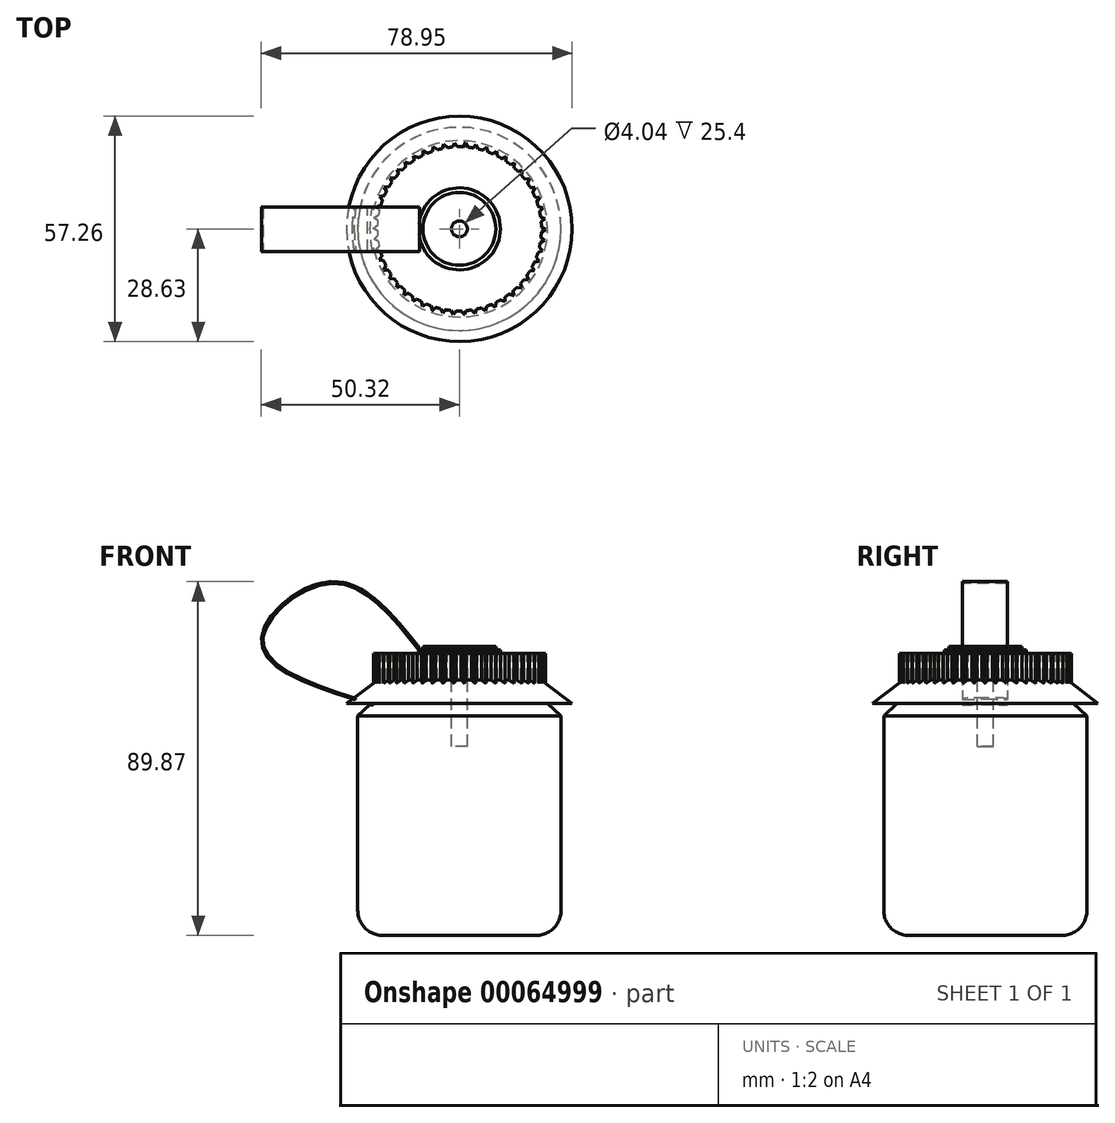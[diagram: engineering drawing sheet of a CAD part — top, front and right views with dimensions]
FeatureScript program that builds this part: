
annotation { "Feature Type Name" : "Feature", "Feature Type Description" : "" }
export const myFeature = defineFeature(function(context is Context, id is Id, definition is map)
    precondition{}
    {
        {
            var Q0;
            Q0=qCreatedBy(makeId("Front.planeOp"),FACE);
            var sketch = newSketch(context, id + "F0", { "sketchPlane" : qUnion([Q0])});
            skLineSegment(sketch, "E0", {"start": v(0, 0) * mm, "end": v(0, -55.76) * mm});
            skLineSegment(sketch, "E1", {"start": v(0, -55.76) * mm, "end": v(-19.47, -55.76) * mm});
            skLineSegment(sketch, "E2", {"start": v(-25.82, -49.41) * mm, "end": v(-25.82, 0) * mm});
            skLineSegment(sketch, "E3", {"start": v(0, 15.82) * mm, "end": v(0, 0) * mm});
            skPoint(sketch, "E4.visualSharp", {"position": v(-25.82, -55.76) * mm});
            skArc(sketch, "E4.filletArc", {"start": v(-25.82, -49.41) * mm, "mid": v(-23.96, -53.9) * mm, "end": v(-19.47, -55.76) * mm});
            skLineSegment(sketch, "E5", {"start": v(-25.82, 0) * mm, "end": v(-22.4, 3.12) * mm});
            skLineSegment(sketch, "E6", {"start": v(-22.4, 3.12) * mm, "end": v(-28.63, 3.12) * mm});
            skLineSegment(sketch, "E7", {"start": v(-28.63, 3.12) * mm, "end": v(-20.78, 9.12) * mm});
            skLineSegment(sketch, "E8", {"start": v(-20.78, 9.12) * mm, "end": v(-20.78, 15.82) * mm});
            skLineSegment(sketch, "E9", {"start": v(-20.78, 15.82) * mm, "end": v(0, 15.82) * mm});
            skSolve(sketch);
        }
        {
            var Q0;
            Q0 = qSketchRegion(id + "F0", true);
            var Q1;
            Q1=sQuery(id+"F0.wireOp",EDGE,"E0");
            revolve(context, id + "F1", {"entities" : qUnion([Q0]), "axis" : qUnion([Q1]), "revolveType" : RevolveType.FULL});
        }
        {
            var Q0;
            Q0=makeQuery(id+"F1.opRevolve","SWEPT_FACE",FACE,{"disambiguationData":[OSD([sQuery(id+"F0.wireOp",EDGE,"E9")])]});
            var sketch = newSketch(context, id + "F2", { "sketchPlane" : qUnion([Q0])});
            skCircle(sketch, "E10", {"center": v(0, 0) * mm, "radius": 20.84 * mm});
            skLineSegment(sketch, "E11", {"start": v(18.63, 9.2) * mm, "end": v(19.22, 10.42) * mm});
            skLineSegment(sketch, "E12", {"start": v(19.22, 10.42) * mm, "end": v(17.98, 10.42) * mm});
            skLineSegment(sketch, "E13.1.0", {"start": v(17.33, 11.47) * mm, "end": v(17.76, 12.75) * mm});
            skLineSegment(sketch, "E13.1.1", {"start": v(17.76, 12.75) * mm, "end": v(16.53, 12.6) * mm});
            skLineSegment(sketch, "E13.2.0", {"start": v(15.76, 13.55) * mm, "end": v(16.03, 14.88) * mm});
            skLineSegment(sketch, "E13.2.1", {"start": v(16.03, 14.88) * mm, "end": v(14.82, 14.57) * mm});
            skLineSegment(sketch, "E13.3.0", {"start": v(13.93, 15.42) * mm, "end": v(14.04, 16.77) * mm});
            skLineSegment(sketch, "E13.3.1", {"start": v(14.04, 16.77) * mm, "end": v(12.88, 16.31) * mm});
            skLineSegment(sketch, "E13.4.0", {"start": v(11.9, 17.04) * mm, "end": v(11.82, 18.4) * mm});
            skLineSegment(sketch, "E13.4.1", {"start": v(11.82, 18.4) * mm, "end": v(10.73, 17.8) * mm});
            skLineSegment(sketch, "E13.5.0", {"start": v(9.66, 18.4) * mm, "end": v(9.42, 19.73) * mm});
            skLineSegment(sketch, "E13.5.1", {"start": v(9.42, 19.73) * mm, "end": v(8.42, 19) * mm});
            skLineSegment(sketch, "E13.6.0", {"start": v(7.28, 19.47) * mm, "end": v(6.88, 20.76) * mm});
            skLineSegment(sketch, "E13.6.1", {"start": v(6.88, 20.76) * mm, "end": v(5.97, 19.9) * mm});
            skLineSegment(sketch, "E13.7.0", {"start": v(4.78, 20.22) * mm, "end": v(4.22, 21.46) * mm});
            skLineSegment(sketch, "E13.7.1", {"start": v(4.22, 21.46) * mm, "end": v(3.43, 20.5) * mm});
            skLineSegment(sketch, "E13.8.0", {"start": v(2.2, 20.66) * mm, "end": v(1.5, 21.82) * mm});
            skLineSegment(sketch, "E13.8.1", {"start": v(1.5, 21.82) * mm, "end": v(0.83, 20.77) * mm});
            skLineSegment(sketch, "E13.9.0", {"start": v(-0.4, 20.78) * mm, "end": v(-1.25, 21.83) * mm});
            skLineSegment(sketch, "E13.9.1", {"start": v(-1.25, 21.83) * mm, "end": v(-1.78, 20.7) * mm});
            skLineSegment(sketch, "E13.10.0", {"start": v(-3, 20.56) * mm, "end": v(-3.97, 21.5) * mm});
            skLineSegment(sketch, "E13.10.1", {"start": v(-3.97, 21.5) * mm, "end": v(-4.36, 20.32) * mm});
            skLineSegment(sketch, "E13.11.0", {"start": v(-5.55, 20.03) * mm, "end": v(-6.64, 20.84) * mm});
            skLineSegment(sketch, "E13.11.1", {"start": v(-6.64, 20.84) * mm, "end": v(-6.87, 19.61) * mm});
            skLineSegment(sketch, "E13.12.0", {"start": v(-8.02, 19.17) * mm, "end": v(-9.2, 19.84) * mm});
            skLineSegment(sketch, "E13.12.1", {"start": v(-9.2, 19.84) * mm, "end": v(-9.27, 18.6) * mm});
            skLineSegment(sketch, "E13.13.0", {"start": v(-10.36, 18.02) * mm, "end": v(-11.61, 18.53) * mm});
            skLineSegment(sketch, "E13.13.1", {"start": v(-11.61, 18.53) * mm, "end": v(-11.53, 17.29) * mm});
            skLineSegment(sketch, "E13.14.0", {"start": v(-12.54, 16.58) * mm, "end": v(-13.84, 16.93) * mm});
            skLineSegment(sketch, "E13.14.1", {"start": v(-13.84, 16.93) * mm, "end": v(-13.6, 15.7) * mm});
            skLineSegment(sketch, "E13.15.0", {"start": v(-14.51, 14.87) * mm, "end": v(-15.85, 15.06) * mm});
            skLineSegment(sketch, "E13.15.1", {"start": v(-15.85, 15.06) * mm, "end": v(-15.47, 13.88) * mm});
            skLineSegment(sketch, "E13.16.0", {"start": v(-16.26, 12.94) * mm, "end": v(-17.62, 12.95) * mm});
            skLineSegment(sketch, "E13.16.1", {"start": v(-17.62, 12.95) * mm, "end": v(-17.09, 11.83) * mm});
            skLineSegment(sketch, "E13.17.0", {"start": v(-17.76, 10.8) * mm, "end": v(-19.1, 10.64) * mm});
            skLineSegment(sketch, "E13.17.1", {"start": v(-19.1, 10.64) * mm, "end": v(-18.43, 9.6) * mm});
            skLineSegment(sketch, "E13.18.0", {"start": v(-18.97, 8.49) * mm, "end": v(-20.29, 8.17) * mm});
            skLineSegment(sketch, "E13.18.1", {"start": v(-20.29, 8.17) * mm, "end": v(-19.5, 7.2) * mm});
            skLineSegment(sketch, "E13.19.0", {"start": v(-19.88, 6.04) * mm, "end": v(-21.15, 5.56) * mm});
            skLineSegment(sketch, "E13.19.1", {"start": v(-21.15, 5.56) * mm, "end": v(-20.24, 4.7) * mm});
            skLineSegment(sketch, "E13.20.0", {"start": v(-20.48, 3.5) * mm, "end": v(-21.68, 2.87) * mm});
            skLineSegment(sketch, "E13.20.1", {"start": v(-21.68, 2.87) * mm, "end": v(-20.67, 2.13) * mm});
            skLineSegment(sketch, "E13.21.0", {"start": v(-20.76, 0.9) * mm, "end": v(-21.87, 0.13) * mm});
            skLineSegment(sketch, "E13.21.1", {"start": v(-21.87, 0.13) * mm, "end": v(-20.78, -0.47) * mm});
            skLineSegment(sketch, "E13.22.0", {"start": v(-20.71, -1.7) * mm, "end": v(-21.71, -2.62) * mm});
            skLineSegment(sketch, "E13.22.1", {"start": v(-21.71, -2.62) * mm, "end": v(-20.55, -3.07) * mm});
            skLineSegment(sketch, "E13.23.0", {"start": v(-20.34, -4.29) * mm, "end": v(-21.21, -5.32) * mm});
            skLineSegment(sketch, "E13.23.1", {"start": v(-21.21, -5.32) * mm, "end": v(-20, -5.63) * mm});
            skLineSegment(sketch, "E13.24.0", {"start": v(-19.64, -6.8) * mm, "end": v(-20.38, -7.93) * mm});
            skLineSegment(sketch, "E13.24.1", {"start": v(-20.38, -7.93) * mm, "end": v(-19.14, -8.09) * mm});
            skLineSegment(sketch, "E13.25.0", {"start": v(-18.63, -9.2) * mm, "end": v(-19.22, -10.42) * mm});
            skLineSegment(sketch, "E13.25.1", {"start": v(-19.22, -10.42) * mm, "end": v(-17.98, -10.42) * mm});
            skLineSegment(sketch, "E13.26.0", {"start": v(-17.33, -11.47) * mm, "end": v(-17.76, -12.75) * mm});
            skLineSegment(sketch, "E13.26.1", {"start": v(-17.76, -12.75) * mm, "end": v(-16.53, -12.6) * mm});
            skLineSegment(sketch, "E13.27.0", {"start": v(-15.76, -13.55) * mm, "end": v(-16.03, -14.88) * mm});
            skLineSegment(sketch, "E13.27.1", {"start": v(-16.03, -14.88) * mm, "end": v(-14.82, -14.57) * mm});
            skLineSegment(sketch, "E13.28.0", {"start": v(-13.93, -15.42) * mm, "end": v(-14.04, -16.77) * mm});
            skLineSegment(sketch, "E13.28.1", {"start": v(-14.04, -16.77) * mm, "end": v(-12.88, -16.31) * mm});
            skLineSegment(sketch, "E13.29.0", {"start": v(-11.9, -17.04) * mm, "end": v(-11.82, -18.4) * mm});
            skLineSegment(sketch, "E13.29.1", {"start": v(-11.82, -18.4) * mm, "end": v(-10.73, -17.8) * mm});
            skLineSegment(sketch, "E13.30.0", {"start": v(-9.66, -18.4) * mm, "end": v(-9.42, -19.73) * mm});
            skLineSegment(sketch, "E13.30.1", {"start": v(-9.42, -19.73) * mm, "end": v(-8.42, -19) * mm});
            skLineSegment(sketch, "E13.31.0", {"start": v(-7.28, -19.47) * mm, "end": v(-6.88, -20.76) * mm});
            skLineSegment(sketch, "E13.31.1", {"start": v(-6.88, -20.76) * mm, "end": v(-5.97, -19.9) * mm});
            skLineSegment(sketch, "E13.32.0", {"start": v(-4.78, -20.22) * mm, "end": v(-4.22, -21.46) * mm});
            skLineSegment(sketch, "E13.32.1", {"start": v(-4.22, -21.46) * mm, "end": v(-3.43, -20.5) * mm});
            skLineSegment(sketch, "E13.33.0", {"start": v(-2.2, -20.66) * mm, "end": v(-1.5, -21.82) * mm});
            skLineSegment(sketch, "E13.33.1", {"start": v(-1.5, -21.82) * mm, "end": v(-0.83, -20.77) * mm});
            skLineSegment(sketch, "E13.34.0", {"start": v(0.4, -20.78) * mm, "end": v(1.25, -21.83) * mm});
            skLineSegment(sketch, "E13.34.1", {"start": v(1.25, -21.83) * mm, "end": v(1.78, -20.7) * mm});
            skLineSegment(sketch, "E13.35.0", {"start": v(3, -20.56) * mm, "end": v(3.97, -21.5) * mm});
            skLineSegment(sketch, "E13.35.1", {"start": v(3.97, -21.5) * mm, "end": v(4.36, -20.32) * mm});
            skLineSegment(sketch, "E13.36.0", {"start": v(5.55, -20.03) * mm, "end": v(6.64, -20.84) * mm});
            skLineSegment(sketch, "E13.36.1", {"start": v(6.64, -20.84) * mm, "end": v(6.87, -19.61) * mm});
            skLineSegment(sketch, "E13.37.0", {"start": v(8.02, -19.17) * mm, "end": v(9.2, -19.84) * mm});
            skLineSegment(sketch, "E13.37.1", {"start": v(9.2, -19.84) * mm, "end": v(9.27, -18.6) * mm});
            skLineSegment(sketch, "E13.38.0", {"start": v(10.36, -18.02) * mm, "end": v(11.61, -18.53) * mm});
            skLineSegment(sketch, "E13.38.1", {"start": v(11.61, -18.53) * mm, "end": v(11.53, -17.29) * mm});
            skLineSegment(sketch, "E13.39.0", {"start": v(12.54, -16.58) * mm, "end": v(13.84, -16.93) * mm});
            skLineSegment(sketch, "E13.39.1", {"start": v(13.84, -16.93) * mm, "end": v(13.6, -15.7) * mm});
            skLineSegment(sketch, "E13.40.0", {"start": v(14.51, -14.87) * mm, "end": v(15.85, -15.06) * mm});
            skLineSegment(sketch, "E13.40.1", {"start": v(15.85, -15.06) * mm, "end": v(15.47, -13.88) * mm});
            skLineSegment(sketch, "E13.41.0", {"start": v(16.26, -12.94) * mm, "end": v(17.62, -12.95) * mm});
            skLineSegment(sketch, "E13.41.1", {"start": v(17.62, -12.95) * mm, "end": v(17.09, -11.83) * mm});
            skLineSegment(sketch, "E13.42.0", {"start": v(17.76, -10.8) * mm, "end": v(19.1, -10.64) * mm});
            skLineSegment(sketch, "E13.42.1", {"start": v(19.1, -10.64) * mm, "end": v(18.43, -9.6) * mm});
            skLineSegment(sketch, "E13.43.0", {"start": v(18.97, -8.49) * mm, "end": v(20.29, -8.17) * mm});
            skLineSegment(sketch, "E13.43.1", {"start": v(20.29, -8.17) * mm, "end": v(19.5, -7.2) * mm});
            skLineSegment(sketch, "E13.44.0", {"start": v(19.88, -6.04) * mm, "end": v(21.15, -5.56) * mm});
            skLineSegment(sketch, "E13.44.1", {"start": v(21.15, -5.56) * mm, "end": v(20.24, -4.7) * mm});
            skLineSegment(sketch, "E14.1.45.0", {"start": v(20.48, -3.5) * mm, "end": v(21.68, -2.87) * mm});
            skLineSegment(sketch, "E14.3.45.0", {"start": v(21.68, -2.87) * mm, "end": v(20.67, -2.13) * mm});
            skLineSegment(sketch, "E14.1.46.0", {"start": v(20.76, -0.9) * mm, "end": v(21.87, -0.13) * mm});
            skLineSegment(sketch, "E14.3.46.0", {"start": v(21.87, -0.13) * mm, "end": v(20.78, 0.47) * mm});
            skLineSegment(sketch, "E14.1.47.0", {"start": v(20.71, 1.7) * mm, "end": v(21.71, 2.62) * mm});
            skLineSegment(sketch, "E14.3.47.0", {"start": v(21.71, 2.62) * mm, "end": v(20.55, 3.07) * mm});
            skLineSegment(sketch, "E15.1.48.0", {"start": v(20.34, 4.29) * mm, "end": v(21.21, 5.32) * mm});
            skLineSegment(sketch, "E15.3.48.0", {"start": v(21.21, 5.32) * mm, "end": v(20, 5.63) * mm});
            skLineSegment(sketch, "E15.1.49.0", {"start": v(19.64, 6.8) * mm, "end": v(20.38, 7.93) * mm});
            skLineSegment(sketch, "E15.3.49.0", {"start": v(20.38, 7.93) * mm, "end": v(19.14, 8.09) * mm});
            skSolve(sketch);
        }
        {
            var Q0;
            Q0 = qSketchRegion(id + "F2", true);
            extrude(context, id + "F3", {"entities" : qUnion([Q0]), "operationType" : NewBodyOperationType.ADD, "oppositeDirection" : true, "depth" : 25.4 * mm});
        }
        {
            var Q0;
            Q0=makeQuery(id+"F3.boolean.opBoolean","MERGE",FACE,{"derivedFrom":[makeQuery(id+"F1.opRevolve","SWEPT_FACE",FACE,{"disambiguationData":[OSD([sQuery(id+"F0.wireOp",EDGE,"E9")])]}),makeQuery(id+"F3.opExtrude","CAP_FACE",FACE,{"disambiguationData":[OSD([sQuery(id+"F2.wireOp",EDGE,"E10"),sQuery(id+"F2.wireOp",EDGE,"E11"),sQuery(id+"F2.wireOp",EDGE,"E12"),sQuery(id+"F2.wireOp",EDGE,"E13.1.0"),sQuery(id+"F2.wireOp",EDGE,"E13.1.1"),sQuery(id+"F2.wireOp",EDGE,"E13.2.0"),sQuery(id+"F2.wireOp",EDGE,"E13.2.1"),sQuery(id+"F2.wireOp",EDGE,"E13.3.0"),sQuery(id+"F2.wireOp",EDGE,"E13.3.1"),sQuery(id+"F2.wireOp",EDGE,"E13.4.0"),sQuery(id+"F2.wireOp",EDGE,"E13.4.1"),sQuery(id+"F2.wireOp",EDGE,"E13.5.0"),sQuery(id+"F2.wireOp",EDGE,"E13.5.1"),sQuery(id+"F2.wireOp",EDGE,"E13.6.0"),sQuery(id+"F2.wireOp",EDGE,"E13.6.1"),sQuery(id+"F2.wireOp",EDGE,"E13.7.0"),sQuery(id+"F2.wireOp",EDGE,"E13.7.1"),sQuery(id+"F2.wireOp",EDGE,"E13.8.0"),sQuery(id+"F2.wireOp",EDGE,"E13.8.1"),sQuery(id+"F2.wireOp",EDGE,"E13.9.0"),sQuery(id+"F2.wireOp",EDGE,"E13.9.1"),sQuery(id+"F2.wireOp",EDGE,"E13.10.0"),sQuery(id+"F2.wireOp",EDGE,"E13.10.1"),sQuery(id+"F2.wireOp",EDGE,"E13.11.0"),sQuery(id+"F2.wireOp",EDGE,"E13.11.1"),sQuery(id+"F2.wireOp",EDGE,"E13.12.0"),sQuery(id+"F2.wireOp",EDGE,"E13.12.1"),sQuery(id+"F2.wireOp",EDGE,"E13.13.0"),sQuery(id+"F2.wireOp",EDGE,"E13.13.1"),sQuery(id+"F2.wireOp",EDGE,"E13.14.0"),sQuery(id+"F2.wireOp",EDGE,"E13.14.1"),sQuery(id+"F2.wireOp",EDGE,"E13.15.0"),sQuery(id+"F2.wireOp",EDGE,"E13.15.1"),sQuery(id+"F2.wireOp",EDGE,"E13.16.0"),sQuery(id+"F2.wireOp",EDGE,"E13.16.1"),sQuery(id+"F2.wireOp",EDGE,"E13.17.0"),sQuery(id+"F2.wireOp",EDGE,"E13.17.1"),sQuery(id+"F2.wireOp",EDGE,"E13.18.0"),sQuery(id+"F2.wireOp",EDGE,"E13.18.1"),sQuery(id+"F2.wireOp",EDGE,"E13.19.0"),sQuery(id+"F2.wireOp",EDGE,"E13.19.1"),sQuery(id+"F2.wireOp",EDGE,"E13.20.0"),sQuery(id+"F2.wireOp",EDGE,"E13.20.1"),sQuery(id+"F2.wireOp",EDGE,"E13.21.0"),sQuery(id+"F2.wireOp",EDGE,"E13.21.1"),sQuery(id+"F2.wireOp",EDGE,"E13.22.0"),sQuery(id+"F2.wireOp",EDGE,"E13.22.1"),sQuery(id+"F2.wireOp",EDGE,"E13.23.0"),sQuery(id+"F2.wireOp",EDGE,"E13.23.1"),sQuery(id+"F2.wireOp",EDGE,"E13.24.0"),sQuery(id+"F2.wireOp",EDGE,"E13.24.1"),sQuery(id+"F2.wireOp",EDGE,"E13.25.0"),sQuery(id+"F2.wireOp",EDGE,"E13.25.1"),sQuery(id+"F2.wireOp",EDGE,"E13.26.0"),sQuery(id+"F2.wireOp",EDGE,"E13.26.1"),sQuery(id+"F2.wireOp",EDGE,"E13.27.0"),sQuery(id+"F2.wireOp",EDGE,"E13.27.1"),sQuery(id+"F2.wireOp",EDGE,"E13.28.0"),sQuery(id+"F2.wireOp",EDGE,"E13.28.1"),sQuery(id+"F2.wireOp",EDGE,"E13.29.0"),sQuery(id+"F2.wireOp",EDGE,"E13.29.1"),sQuery(id+"F2.wireOp",EDGE,"E13.30.0"),sQuery(id+"F2.wireOp",EDGE,"E13.30.1"),sQuery(id+"F2.wireOp",EDGE,"E13.31.0"),sQuery(id+"F2.wireOp",EDGE,"E13.31.1"),sQuery(id+"F2.wireOp",EDGE,"E13.32.0"),sQuery(id+"F2.wireOp",EDGE,"E13.32.1"),sQuery(id+"F2.wireOp",EDGE,"E13.33.0"),sQuery(id+"F2.wireOp",EDGE,"E13.33.1"),sQuery(id+"F2.wireOp",EDGE,"E13.34.0"),sQuery(id+"F2.wireOp",EDGE,"E13.34.1"),sQuery(id+"F2.wireOp",EDGE,"E13.35.0"),sQuery(id+"F2.wireOp",EDGE,"E13.35.1"),sQuery(id+"F2.wireOp",EDGE,"E13.36.0"),sQuery(id+"F2.wireOp",EDGE,"E13.36.1"),sQuery(id+"F2.wireOp",EDGE,"E13.37.0"),sQuery(id+"F2.wireOp",EDGE,"E13.37.1"),sQuery(id+"F2.wireOp",EDGE,"E13.38.0"),sQuery(id+"F2.wireOp",EDGE,"E13.38.1"),sQuery(id+"F2.wireOp",EDGE,"E13.39.0"),sQuery(id+"F2.wireOp",EDGE,"E13.39.1"),sQuery(id+"F2.wireOp",EDGE,"E13.40.0"),sQuery(id+"F2.wireOp",EDGE,"E13.40.1"),sQuery(id+"F2.wireOp",EDGE,"E13.41.0"),sQuery(id+"F2.wireOp",EDGE,"E13.41.1"),sQuery(id+"F2.wireOp",EDGE,"E13.42.0"),sQuery(id+"F2.wireOp",EDGE,"E13.42.1"),sQuery(id+"F2.wireOp",EDGE,"E13.43.0"),sQuery(id+"F2.wireOp",EDGE,"E13.43.1"),sQuery(id+"F2.wireOp",EDGE,"E13.44.0"),sQuery(id+"F2.wireOp",EDGE,"E13.44.1"),sQuery(id+"F2.wireOp",EDGE,"E14.1.45.0"),sQuery(id+"F2.wireOp",EDGE,"E14.3.45.0"),sQuery(id+"F2.wireOp",EDGE,"E14.1.46.0"),sQuery(id+"F2.wireOp",EDGE,"E14.3.46.0"),sQuery(id+"F2.wireOp",EDGE,"E14.1.47.0"),sQuery(id+"F2.wireOp",EDGE,"E14.3.47.0"),sQuery(id+"F2.wireOp",EDGE,"E15.1.48.0"),sQuery(id+"F2.wireOp",EDGE,"E15.3.48.0"),sQuery(id+"F2.wireOp",EDGE,"E15.1.49.0"),sQuery(id+"F2.wireOp",EDGE,"E15.3.49.0")])],"isStart":true})]});
            var sketch = newSketch(context, id + "F4", { "sketchPlane" : qUnion([Q0])});
            skCircle(sketch, "E16", {"center": v(0, 0) * mm, "radius": 10.42 * mm});
            skSolve(sketch);
        }
        {
            var Q0;
            Q0 = qSketchRegion(id + "F4", true);
            extrude(context, id + "F5", {"entities" : qUnion([Q0]), "operationType" : NewBodyOperationType.ADD, "depth" : 0.92 * mm});
        }
        {
            var Q0;
            Q0=makeQuery(id+"F5.opExtrude","CAP_FACE",FACE,{"disambiguationData":[OSD([sQuery(id+"F4.wireOp",EDGE,"E16")])],"isStart":false});
            var sketch = newSketch(context, id + "F6", { "sketchPlane" : qUnion([Q0])});
            skCircle(sketch, "E17", {"center": v(0, 0) * mm, "radius": 9.26 * mm});
            skSolve(sketch);
        }
        {
            var Q0;
            Q0 = qSketchRegion(id + "F6", true);
            extrude(context, id + "F7", {"entities" : qUnion([Q0]), "operationType" : NewBodyOperationType.ADD, "depth" : 0.91 * mm});
        }
        {
            var Q0;
            Q0=makeQuery(id+"F7.opExtrude","CAP_FACE",FACE,{"disambiguationData":[OSD([sQuery(id+"F6.wireOp",EDGE,"E17")])],"isStart":false});
            var sketch = newSketch(context, id + "F8", { "sketchPlane" : qUnion([Q0])});
            skCircle(sketch, "E18", {"center": v(0, 0) * mm, "radius": 2.02 * mm});
            skSolve(sketch);
        }
        {
            var Q0;
            Q0 = qSketchRegion(id + "F8", true);
            extrude(context, id + "F9", {"entities" : qUnion([Q0]), "operationType" : NewBodyOperationType.REMOVE, "oppositeDirection" : true, "depth" : 25.4 * mm});
        }
        {
            var Q0;
            Q0=qCreatedBy(makeId("Right.planeOp"),FACE);
            cPlane(context, id + "F10", {"entities" : qUnion([Q0]), "cplaneType" : CPlaneType.OFFSET, "offset" : 10.16 * mm, "oppositeDirection" : true, "width" : 152.4 * mm, "height" : 152.4 * mm});
        }
        {
            var Q0;
            Q0=qCreatedBy(id+"F10.planeOp",FACE);
            var sketch = newSketch(context, id + "F11", { "sketchPlane" : qUnion([Q0])});
            skLineSegment(sketch, "E19.bottom", {"start": v(5.54, 16.51) * mm, "end": v(-5.77, 16.51) * mm});
            skLineSegment(sketch, "E19.top", {"start": v(5.54, 17.2) * mm, "end": v(-5.77, 17.2) * mm});
            skLineSegment(sketch, "E19.left", {"start": v(5.54, 16.51) * mm, "end": v(5.54, 17.2) * mm});
            skLineSegment(sketch, "E19.right", {"start": v(-5.77, 16.51) * mm, "end": v(-5.77, 17.2) * mm});
            skSolve(sketch);
        }
        {
            var Q0;
            Q0=qCreatedBy(makeId("Front.planeOp"),FACE);
            var sketch = newSketch(context, id + "F12", { "sketchPlane" : qUnion([Q0])});
            skFitSpline(sketch, "E20", {"points": [v(-10.2, 16.95) * mm, v(-32.92, 33.89) * mm, v(-50.12, 18.84) * mm, v(-19.63, 2.2) * mm], "startDerivative": vector(-62.53, 79.4) * mm, "endDerivative": vector(122.93, -36.69) * mm});
            skSolve(sketch);
        }
        {
            var Q0;
            Q0 = qSketchRegion(id + "F11", true);
            var Q1;
            Q1 = qConstructionFilter(qBodyType(qCreatedBy(id + "F12" ,EDGE), BodyType.WIRE), ConstructionObject.NO);
            sweep(context, id + "F13", {"operationType" : NewBodyOperationType.ADD, "profiles" : qUnion([Q0]), "path" : qUnion([Q1])});
        }
    });
